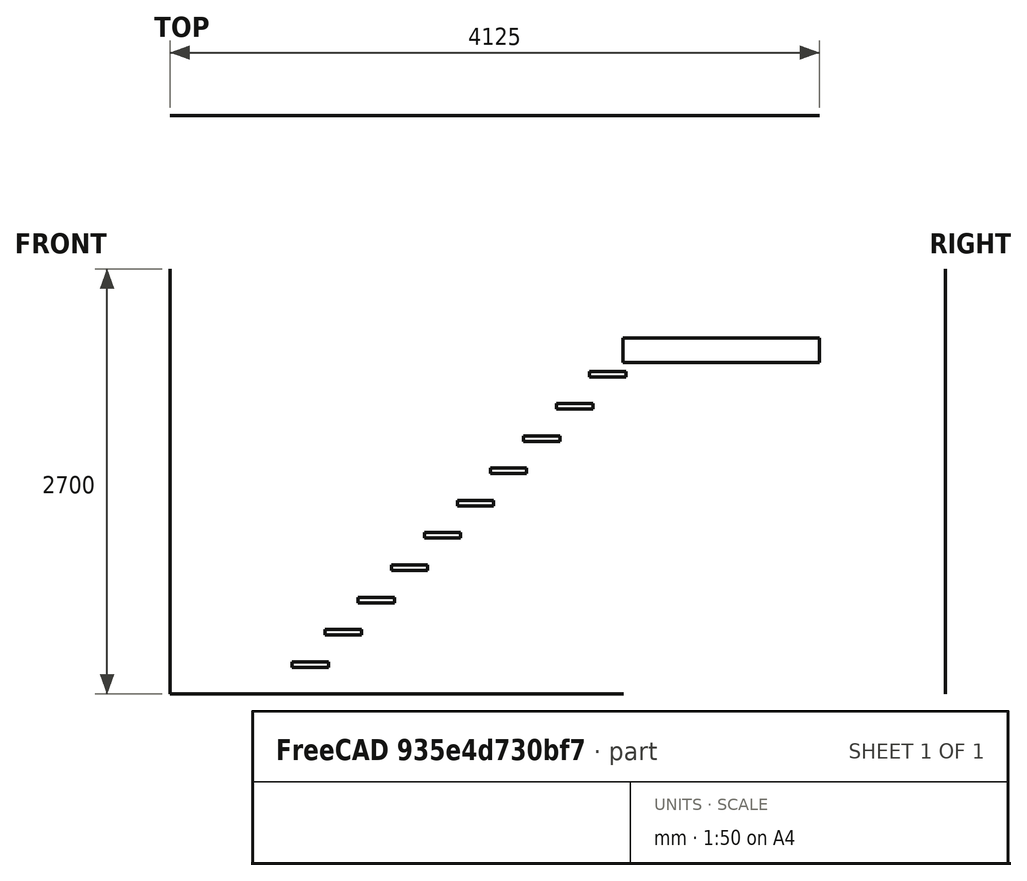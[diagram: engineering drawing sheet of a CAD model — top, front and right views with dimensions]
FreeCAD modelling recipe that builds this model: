
FCSTD DOCUMENT  (FreeCAD 0.17R10949 (Git))
Label: stair_profile
License: All rights reserved
LicenseURL: http://en.wikipedia.org/wiki/All_rights_reserved
objects: Part::Part2DObjectPython×5, Part::FeaturePython×1, Part::Compound×1
note: 7 computed .brp shape members not serialized (recipe doc carries the construction recipe); baked Part::Feature solids carry a one-line shape summary decoded from their .brp

FEATURE [Part::Part2DObjectPython] Line  # Draft 2D object (typed FeaturePython)
  ChamferSize = 0
  Closed = false
  End = (2105,0,0)
  FilletRadius = 0
  Length = 2105
  MakeFace = true
  Points = (2) [(0,0,0),(2105,0,1.28894e-13)]
  Start = (0,0,0)
  Subdivisions = 0
FEATURE [Part::Part2DObjectPython] Rectangle  # Draft 2D object (typed FeaturePython)
  ChamferSize = 0
  Columns = 1
  FilletRadius = 0
  Height = -35
  Length = 230
  MakeFace = true
  Placement = pos=(0,0,205) rot=(1,0,0;1.5708rad)
  Rows = 1
FEATURE [Part::FeaturePython] Array  # Draft array (typed FeaturePython)
  Angle = 360
  ArrayType = 0
  Axis = (0,0,1)
  Base = -> Rectangle
  Center = (0,0,0)
  Fuse = false
  IntervalAxis = (0,0,0)
  IntervalX = (210,0,205)
  IntervalY = (0,0,0)
  IntervalZ = (0,0,0)
  NumberPolar = 1
  NumberX = 10
  NumberY = 1
  NumberZ = 1
FEATURE [Part::Part2DObjectPython] Line001  # Draft 2D object (typed FeaturePython)
  ChamferSize = 0
  Closed = false
  End = (-775,0,0)
  FilletRadius = 0
  Length = 775
  MakeFace = true
  Points = (2) [(0,0,0),(-775,0,-4.74551e-14)]
  Start = (0,0,0)
  Subdivisions = 0
  expr: Length = 2880 * 1mm - Line.Length
FEATURE [Part::Part2DObjectPython] Rectangle001  # Draft 2D object (typed FeaturePython)
  ChamferSize = 0
  Columns = 1
  FilletRadius = 0
  Height = 155
  Length = 1250
  MakeFace = true
  Placement = pos=(2100,0,2105) rot=(1,0,0;1.5708rad)
  Rows = 1
FEATURE [Part::Part2DObjectPython] Line002  # Draft 2D object (typed FeaturePython)
  ChamferSize = 0
  Closed = false
  End = (-775,0,2700)
  FilletRadius = 0
  Length = 2700
  MakeFace = true
  Points = (2) [(-775,0,-4.74551e-14),(-775,0,2700)]
  Start = (-775,0,0)
  Subdivisions = 0
FEATURE [Part::Compound] Compound
  Links = -> [Line,Array,Line001,Rectangle001,Line002,Rectangle]
